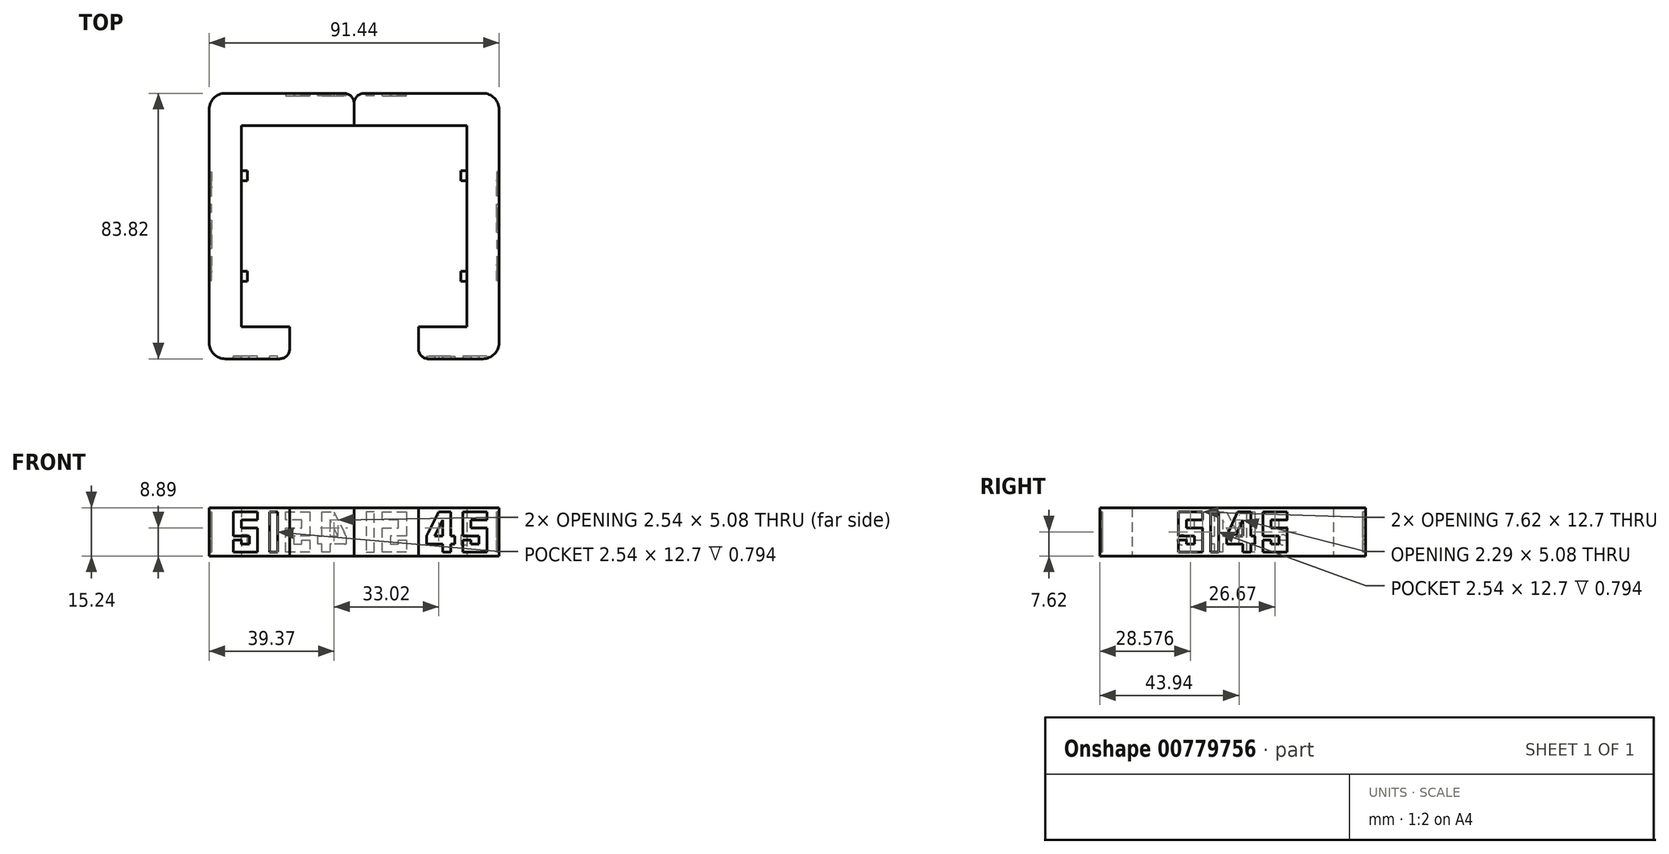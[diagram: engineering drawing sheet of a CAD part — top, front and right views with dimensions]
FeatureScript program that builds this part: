
annotation { "Feature Type Name" : "Feature", "Feature Type Description" : "" }
export const myFeature = defineFeature(function(context is Context, id is Id, definition is map)
    precondition{}
    {
        {
            var Q0;
            Q0=qCreatedBy(makeId("Top.planeOp"),FACE);
            var sketch = newSketch(context, id + "F0", { "sketchPlane" : qUnion([Q0])});
            skLineSegment(sketch, "E0", {"start": v(0, 28.67) * mm, "end": v(0, 38.83) * mm});
            skLineSegment(sketch, "E1", {"start": v(0, 38.83) * mm, "end": v(45.72, 38.83) * mm});
            skLineSegment(sketch, "E2", {"start": v(45.72, 38.83) * mm, "end": v(45.72, -44.99) * mm});
            skLineSegment(sketch, "E3", {"start": v(45.72, -44.99) * mm, "end": v(20.32, -44.99) * mm});
            skLineSegment(sketch, "E4", {"start": v(20.32, -44.99) * mm, "end": v(20.32, -34.83) * mm});
            skLineSegment(sketch, "E5", {"start": v(20.32, -34.83) * mm, "end": v(35.56, -34.83) * mm});
            skLineSegment(sketch, "E6", {"start": v(35.56, -34.83) * mm, "end": v(35.56, 28.67) * mm});
            skLineSegment(sketch, "E7", {"start": v(35.56, 28.67) * mm, "end": v(0, 28.67) * mm});
            skSolve(sketch);
        }
        {
            var Q0;
            Q0=makeQuery(id+"F0.imprint","IMPRINT",FACE,{"disambiguationData":[TD([[makeQuery(id+"F0.imprint","IMPRINT",EDGE,{"derivedFrom":sQuery(id+"F0.wireOp",EDGE,"E0")}),-1.0]])]});
            extrude(context, id + "F1", {"entities" : qUnion([Q0]), "depth" : 15.24 * mm, "offsetDistance" : 25.4 * mm});
        }
        {
            var Q0;
            Q0=makeQuery(id+"F1.opExtrude","SWEPT_FACE",FACE,{"disambiguationData":[OSD([sQuery(id+"F0.wireOp",EDGE,"E6")])]});
            var sketch = newSketch(context, id + "F2", { "sketchPlane" : qUnion([Q0])});
            skCircle(sketch, "E8", {"center": v(-12.8, 5.08) * mm, "radius": 1.59 * mm});
            skPoint(sketch, "E8.centerSnap0", {"position": v(-28.67, 5.08) * mm});
            skCircle(sketch, "E9", {"center": v(18.95, 5.08) * mm, "radius": 1.59 * mm});
            skPoint(sketch, "E9.centerSnap0", {"position": v(34.83, 5.08) * mm});
            skSolve(sketch);
        }
        {
            var Q0;
            Q0=makeQuery(id+"F2.imprint","IMPRINT",FACE,{"disambiguationData":[TD([[makeQuery(id+"F2.imprint","IMPRINT",EDGE,{"derivedFrom":sQuery(id+"F2.wireOp",EDGE,"E8")}),1.0]])]});
            var Q1;
            Q1=makeQuery(id+"F2.imprint","IMPRINT",FACE,{"disambiguationData":[TD([[makeQuery(id+"F2.imprint","IMPRINT",EDGE,{"derivedFrom":sQuery(id+"F2.wireOp",EDGE,"E9")}),1.0]])]});
            extrude(context, id + "F3", {"entities" : qUnion([Q0, Q1]), "operationType" : NewBodyOperationType.ADD, "depth" : 1.9 * mm, "offsetDistance" : 25.4 * mm});
        }
        {
            var Q0;
            Q0=qCreatedBy(makeId("Top.planeOp"),FACE);
            var sketch = newSketch(context, id + "F4", { "sketchPlane" : qUnion([Q0])});
            skLineSegment(sketch, "E10", {"start": v(0, 28.67) * mm, "end": v(-35.56, 28.67) * mm});
            skLineSegment(sketch, "E11", {"start": v(-35.56, 28.67) * mm, "end": v(-35.56, -34.83) * mm});
            skLineSegment(sketch, "E12", {"start": v(-35.56, -34.83) * mm, "end": v(-20.32, -34.83) * mm});
            skLineSegment(sketch, "E13", {"start": v(-20.32, -34.83) * mm, "end": v(-20.32, -44.99) * mm});
            skLineSegment(sketch, "E14", {"start": v(-20.32, -44.99) * mm, "end": v(-45.72, -44.99) * mm});
            skLineSegment(sketch, "E15", {"start": v(-45.72, -44.99) * mm, "end": v(-45.72, 38.83) * mm});
            skLineSegment(sketch, "E16", {"start": v(-45.72, 38.83) * mm, "end": v(0, 38.83) * mm});
            skLineSegment(sketch, "E17", {"start": v(0, 38.83) * mm, "end": v(0, 28.67) * mm});
            skSolve(sketch);
        }
        {
            var Q0;
            Q0=makeQuery(id+"F4.imprint","IMPRINT",FACE,{"disambiguationData":[TD([[makeQuery(id+"F4.imprint","IMPRINT",EDGE,{"derivedFrom":sQuery(id+"F4.wireOp",EDGE,"E10")}),-1.0]])]});
            extrude(context, id + "F5", {"entities" : qUnion([Q0]), "depth" : 15.24 * mm, "offsetDistance" : 25.4 * mm});
        }
        {
            var Q0;
            Q0=makeQuery(id+"F5.opExtrude","SWEPT_FACE",FACE,{"disambiguationData":[OSD([sQuery(id+"F4.wireOp",EDGE,"E11")])]});
            var sketch = newSketch(context, id + "F6", { "sketchPlane" : qUnion([Q0])});
            skCircle(sketch, "E18", {"center": v(-18.95, 5.08) * mm, "radius": 1.59 * mm});
            skPoint(sketch, "E18.centerSnap0", {"position": v(-34.83, 7.62) * mm});
            skCircle(sketch, "E19", {"center": v(12.8, 5.08) * mm, "radius": 1.59 * mm});
            skSolve(sketch);
        }
        {
            var Q0;
            Q0=makeQuery(id+"F6.imprint","IMPRINT",FACE,{"disambiguationData":[TD([[makeQuery(id+"F6.imprint","IMPRINT",EDGE,{"derivedFrom":sQuery(id+"F6.wireOp",EDGE,"E19")}),1.0]])]});
            var Q1;
            Q1=makeQuery(id+"F6.imprint","IMPRINT",FACE,{"disambiguationData":[TD([[makeQuery(id+"F6.imprint","IMPRINT",EDGE,{"derivedFrom":sQuery(id+"F6.wireOp",EDGE,"E18")}),1.0]])]});
            extrude(context, id + "F7", {"entities" : qUnion([Q0, Q1]), "operationType" : NewBodyOperationType.ADD, "depth" : 1.9 * mm, "offsetDistance" : 25.4 * mm});
        }
        {
            var Q0;
            Q0=makeQuery(id+"F1.opExtrude","SWEPT_FACE",FACE,{"disambiguationData":[OSD([sQuery(id+"F0.wireOp",EDGE,"E2")])]});
            var sketch = newSketch(context, id + "F8", { "sketchPlane" : qUnion([Q0])});
            skLineSegment(sketch, "E20", {"start": v(-12.6, 13.97) * mm, "end": v(-20.22, 13.97) * mm});
            skLineSegment(sketch, "E21", {"start": v(-20.22, 13.97) * mm, "end": v(-20.22, 6.35) * mm});
            skLineSegment(sketch, "E22", {"start": v(-20.22, 6.35) * mm, "end": v(-15.14, 6.35) * mm});
            skLineSegment(sketch, "E23", {"start": v(-15.14, 6.35) * mm, "end": v(-15.14, 3.81) * mm});
            skLineSegment(sketch, "E24", {"start": v(-15.14, 3.8) * mm, "end": v(-17.68, 3.8) * mm});
            skLineSegment(sketch, "E25", {"start": v(-17.68, 3.81) * mm, "end": v(-17.68, 5.08) * mm});
            skLineSegment(sketch, "E26", {"start": v(-17.68, 5.08) * mm, "end": v(-20.22, 5.08) * mm});
            skLineSegment(sketch, "E27", {"start": v(-20.22, 5.08) * mm, "end": v(-20.22, 1.27) * mm});
            skLineSegment(sketch, "E28", {"start": v(-20.22, 1.27) * mm, "end": v(-12.6, 1.27) * mm});
            skLineSegment(sketch, "E29", {"start": v(-12.6, 1.27) * mm, "end": v(-12.6, 8.9) * mm});
            skLineSegment(sketch, "E30", {"start": v(-12.6, 8.89) * mm, "end": v(-17.68, 8.89) * mm});
            skLineSegment(sketch, "E31", {"start": v(-17.68, 8.9) * mm, "end": v(-17.68, 11.43) * mm});
            skLineSegment(sketch, "E32", {"start": v(-17.68, 11.43) * mm, "end": v(-12.6, 11.43) * mm});
            skLineSegment(sketch, "E33", {"start": v(-12.6, 11.43) * mm, "end": v(-12.6, 13.97) * mm});
            skLineSegment(sketch, "E34", {"start": v(-10.06, 13.97) * mm, "end": v(-10.06, 1.27) * mm});
            skLineSegment(sketch, "E35", {"start": v(-10.06, 1.27) * mm, "end": v(-7.52, 1.27) * mm});
            skLineSegment(sketch, "E36", {"start": v(-7.52, 1.27) * mm, "end": v(-7.52, 13.97) * mm});
            skLineSegment(sketch, "E37", {"start": v(-7.52, 13.97) * mm, "end": v(-10.06, 13.97) * mm});
            skLineSegment(sketch, "E38", {"start": v(-1.54, 13.97) * mm, "end": v(-4.98, 6.35) * mm});
            skLineSegment(sketch, "E39", {"start": v(-4.98, 6.35) * mm, "end": v(-4.98, 3.81) * mm});
            skLineSegment(sketch, "E40", {"start": v(-4.98, 3.81) * mm, "end": v(0.1, 3.81) * mm});
            skLineSegment(sketch, "E41", {"start": v(0.1, 3.81) * mm, "end": v(0.1, 1.27) * mm});
            skLineSegment(sketch, "E42", {"start": v(0.1, 1.27) * mm, "end": v(2.64, 1.27) * mm});
            skLineSegment(sketch, "E43", {"start": v(2.64, 1.27) * mm, "end": v(2.64, 3.81) * mm});
            skLineSegment(sketch, "E44", {"start": v(2.64, 3.81) * mm, "end": v(3.9, 3.81) * mm});
            skLineSegment(sketch, "E45", {"start": v(3.9, 3.81) * mm, "end": v(3.9, 6.35) * mm});
            skLineSegment(sketch, "E46", {"start": v(3.9, 6.35) * mm, "end": v(2.64, 6.35) * mm});
            skLineSegment(sketch, "E47", {"start": v(2.64, 6.35) * mm, "end": v(2.64, 13.97) * mm});
            skLineSegment(sketch, "E48", {"start": v(2.64, 13.97) * mm, "end": v(-1.54, 13.97) * mm});
            skLineSegment(sketch, "E49", {"start": v(0.1, 6.35) * mm, "end": v(-2.2, 6.35) * mm});
            skLineSegment(sketch, "E50", {"start": v(-2.2, 6.35) * mm, "end": v(0.1, 11.43) * mm});
            skLineSegment(sketch, "E51", {"start": v(0.1, 11.43) * mm, "end": v(0.1, 6.35) * mm});
            skLineSegment(sketch, "E52", {"start": v(14.07, 13.97) * mm, "end": v(6.45, 13.97) * mm});
            skLineSegment(sketch, "E53", {"start": v(6.45, 13.97) * mm, "end": v(6.45, 6.35) * mm});
            skLineSegment(sketch, "E54", {"start": v(6.45, 6.35) * mm, "end": v(11.53, 6.35) * mm});
            skLineSegment(sketch, "E55", {"start": v(11.53, 6.35) * mm, "end": v(11.53, 3.81) * mm});
            skLineSegment(sketch, "E56", {"start": v(11.53, 3.81) * mm, "end": v(8.99, 3.81) * mm});
            skPoint(sketch, "E56.endSnap0", {"position": v(8.99, 6.35) * mm});
            skLineSegment(sketch, "E57", {"start": v(8.99, 3.81) * mm, "end": v(8.99, 5.08) * mm});
            skPoint(sketch, "E57.endSnap0", {"position": v(11.53, 5.08) * mm});
            skLineSegment(sketch, "E58", {"start": v(8.99, 5.08) * mm, "end": v(6.45, 5.08) * mm});
            skLineSegment(sketch, "E59", {"start": v(6.45, 5.08) * mm, "end": v(6.45, 1.27) * mm});
            skLineSegment(sketch, "E60", {"start": v(6.45, 1.27) * mm, "end": v(14.07, 1.27) * mm});
            skLineSegment(sketch, "E61", {"start": v(14.07, 1.27) * mm, "end": v(14.07, 8.9) * mm});
            skLineSegment(sketch, "E62", {"start": v(14.07, 8.9) * mm, "end": v(8.99, 8.9) * mm});
            skLineSegment(sketch, "E63", {"start": v(8.99, 8.9) * mm, "end": v(8.99, 11.43) * mm});
            skLineSegment(sketch, "E64", {"start": v(8.99, 11.43) * mm, "end": v(14.07, 11.43) * mm});
            skLineSegment(sketch, "E65", {"start": v(14.07, 11.43) * mm, "end": v(14.07, 13.97) * mm});
            skLineSegment(sketch, "E66", {"start": v(-20.22, 13.97) * mm, "end": v(-44.99, 13.97) * mm});
            skLineSegment(sketch, "E67", {"start": v(14.07, 13.97) * mm, "end": v(38.83, 13.97) * mm});
            skSolve(sketch);
        }
        {
            var Q0;
            Q0=makeQuery(id+"F8.imprint","IMPRINT",FACE,{"disambiguationData":[TD([[makeQuery(id+"F8.imprint","IMPRINT",EDGE,{"derivedFrom":sQuery(id+"F8.wireOp",EDGE,"E20")}),1.0]])]});
            var Q1;
            Q1=makeQuery(id+"F8.imprint","IMPRINT",FACE,{"disambiguationData":[TD([[makeQuery(id+"F8.imprint","IMPRINT",EDGE,{"derivedFrom":sQuery(id+"F8.wireOp",EDGE,"E34")}),1.0]])]});
            var Q2;
            Q2=makeQuery(id+"F8.imprint","IMPRINT",FACE,{"disambiguationData":[TD([[makeQuery(id+"F8.imprint","IMPRINT",EDGE,{"derivedFrom":sQuery(id+"F8.wireOp",EDGE,"E38")}),1.0]])]});
            var Q3;
            Q3=makeQuery(id+"F8.imprint","IMPRINT",FACE,{"disambiguationData":[TD([[makeQuery(id+"F8.imprint","IMPRINT",EDGE,{"derivedFrom":sQuery(id+"F8.wireOp",EDGE,"E52")}),1.0]])]});
            extrude(context, id + "F9", {"entities" : qUnion([Q0, Q1, Q2, Q3]), "operationType" : NewBodyOperationType.REMOVE, "oppositeDirection" : true, "depth" : 0.8 * mm, "offsetDistance" : 25.4 * mm});
        }
        {
            var Q0;
            Q0=makeQuery(id+"F1.opExtrude","SWEPT_FACE",FACE,{"disambiguationData":[OSD([sQuery(id+"F0.wireOp",EDGE,"E3")])]});
            var sketch = newSketch(context, id + "F10", { "sketchPlane" : qUnion([Q0])});
            skLineSegment(sketch, "E68", {"start": v(22.86, 6.35) * mm, "end": v(22.86, 3.81) * mm});
            skLineSegment(sketch, "E69", {"start": v(22.86, 3.81) * mm, "end": v(27.94, 3.81) * mm});
            skLineSegment(sketch, "E70", {"start": v(27.94, 3.81) * mm, "end": v(27.94, 1.27) * mm});
            skLineSegment(sketch, "E71", {"start": v(27.94, 1.27) * mm, "end": v(30.48, 1.27) * mm});
            skLineSegment(sketch, "E72", {"start": v(30.48, 1.27) * mm, "end": v(30.48, 3.81) * mm});
            skLineSegment(sketch, "E73", {"start": v(30.48, 3.81) * mm, "end": v(31.75, 3.81) * mm});
            skLineSegment(sketch, "E74", {"start": v(31.75, 3.81) * mm, "end": v(31.75, 6.35) * mm});
            skLineSegment(sketch, "E75", {"start": v(31.75, 6.35) * mm, "end": v(30.48, 6.35) * mm});
            skLineSegment(sketch, "E76", {"start": v(30.48, 6.35) * mm, "end": v(30.48, 13.97) * mm});
            skLineSegment(sketch, "E77", {"start": v(30.48, 13.97) * mm, "end": v(26.67, 13.97) * mm});
            skLineSegment(sketch, "E78", {"start": v(26.67, 13.97) * mm, "end": v(22.86, 6.35) * mm});
            skLineSegment(sketch, "E79", {"start": v(27.94, 6.35) * mm, "end": v(25.4, 6.35) * mm});
            skLineSegment(sketch, "E80", {"start": v(25.4, 6.35) * mm, "end": v(27.94, 11.43) * mm});
            skLineSegment(sketch, "E81", {"start": v(27.94, 11.43) * mm, "end": v(27.94, 6.35) * mm});
            skLineSegment(sketch, "E82", {"start": v(41.91, 13.97) * mm, "end": v(34.3, 13.97) * mm});
            skLineSegment(sketch, "E83", {"start": v(34.3, 13.97) * mm, "end": v(34.3, 6.35) * mm});
            skLineSegment(sketch, "E84", {"start": v(34.3, 6.35) * mm, "end": v(39.37, 6.35) * mm});
            skLineSegment(sketch, "E85", {"start": v(39.37, 6.35) * mm, "end": v(39.37, 3.81) * mm});
            skLineSegment(sketch, "E86", {"start": v(39.37, 3.81) * mm, "end": v(36.83, 3.81) * mm});
            skPoint(sketch, "E86.endSnap0", {"position": v(36.83, 6.35) * mm});
            skLineSegment(sketch, "E87", {"start": v(36.83, 3.81) * mm, "end": v(36.83, 5.08) * mm});
            skPoint(sketch, "E87.endSnap0", {"position": v(39.37, 5.08) * mm});
            skLineSegment(sketch, "E88", {"start": v(36.83, 5.08) * mm, "end": v(34.3, 5.08) * mm});
            skLineSegment(sketch, "E89", {"start": v(34.3, 5.08) * mm, "end": v(34.3, 1.27) * mm});
            skLineSegment(sketch, "E90", {"start": v(34.3, 1.27) * mm, "end": v(41.91, 1.27) * mm});
            skLineSegment(sketch, "E91", {"start": v(41.91, 1.27) * mm, "end": v(41.91, 8.89) * mm});
            skLineSegment(sketch, "E92", {"start": v(41.91, 8.89) * mm, "end": v(36.83, 8.89) * mm});
            skLineSegment(sketch, "E93", {"start": v(36.83, 8.89) * mm, "end": v(36.83, 11.43) * mm});
            skLineSegment(sketch, "E94", {"start": v(36.83, 11.43) * mm, "end": v(41.91, 11.43) * mm});
            skLineSegment(sketch, "E95", {"start": v(41.91, 11.43) * mm, "end": v(41.91, 13.97) * mm});
            skSolve(sketch);
        }
        {
            var Q0;
            Q0=makeQuery(id+"F10.imprint","IMPRINT",FACE,{"disambiguationData":[TD([[makeQuery(id+"F10.imprint","IMPRINT",EDGE,{"derivedFrom":sQuery(id+"F10.wireOp",EDGE,"E68")}),1.0]])]});
            var Q1;
            Q1=makeQuery(id+"F10.imprint","IMPRINT",FACE,{"disambiguationData":[TD([[makeQuery(id+"F10.imprint","IMPRINT",EDGE,{"derivedFrom":sQuery(id+"F10.wireOp",EDGE,"E82")}),1.0]])]});
            extrude(context, id + "F11", {"entities" : qUnion([Q0, Q1]), "operationType" : NewBodyOperationType.REMOVE, "oppositeDirection" : true, "depth" : 0.8 * mm, "offsetDistance" : 25.4 * mm});
        }
        {
            var Q0;
            Q0=makeQuery(id+"F5.opExtrude","SWEPT_FACE",FACE,{"disambiguationData":[OSD([sQuery(id+"F4.wireOp",EDGE,"E14")])]});
            var sketch = newSketch(context, id + "F12", { "sketchPlane" : qUnion([Q0])});
            skLineSegment(sketch, "E96", {"start": v(-24.13, 13.97) * mm, "end": v(-26.67, 13.97) * mm});
            skLineSegment(sketch, "E97", {"start": v(-26.67, 13.97) * mm, "end": v(-26.67, 1.27) * mm});
            skLineSegment(sketch, "E98", {"start": v(-26.67, 1.27) * mm, "end": v(-24.13, 1.27) * mm});
            skLineSegment(sketch, "E99", {"start": v(-24.13, 1.27) * mm, "end": v(-24.13, 13.97) * mm});
            skLineSegment(sketch, "E100", {"start": v(-30.48, 13.97) * mm, "end": v(-38.1, 13.97) * mm});
            skLineSegment(sketch, "E101", {"start": v(-38.1, 13.97) * mm, "end": v(-38.1, 6.35) * mm});
            skLineSegment(sketch, "E102", {"start": v(-38.1, 6.35) * mm, "end": v(-33.02, 6.35) * mm});
            skLineSegment(sketch, "E103", {"start": v(-33.02, 6.35) * mm, "end": v(-33.02, 3.8) * mm});
            skLineSegment(sketch, "E104", {"start": v(-33.02, 3.8) * mm, "end": v(-35.56, 3.8) * mm});
            skLineSegment(sketch, "E105", {"start": v(-35.56, 3.8) * mm, "end": v(-35.56, 5.08) * mm});
            skLineSegment(sketch, "E106", {"start": v(-35.56, 5.08) * mm, "end": v(-38.1, 5.08) * mm});
            skLineSegment(sketch, "E107", {"start": v(-38.1, 5.08) * mm, "end": v(-38.1, 1.27) * mm});
            skLineSegment(sketch, "E108", {"start": v(-38.1, 1.27) * mm, "end": v(-30.48, 1.27) * mm});
            skLineSegment(sketch, "E109", {"start": v(-30.48, 1.27) * mm, "end": v(-30.48, 8.9) * mm});
            skLineSegment(sketch, "E110", {"start": v(-30.48, 8.89) * mm, "end": v(-35.56, 8.89) * mm});
            skLineSegment(sketch, "E111", {"start": v(-35.56, 8.89) * mm, "end": v(-35.56, 11.43) * mm});
            skLineSegment(sketch, "E112", {"start": v(-35.56, 11.43) * mm, "end": v(-30.48, 11.43) * mm});
            skLineSegment(sketch, "E113", {"start": v(-30.48, 11.43) * mm, "end": v(-30.48, 13.97) * mm});
            skSolve(sketch);
        }
        {
            var Q0;
            Q0=makeQuery(id+"F12.imprint","IMPRINT",FACE,{"disambiguationData":[TD([[makeQuery(id+"F12.imprint","IMPRINT",EDGE,{"derivedFrom":sQuery(id+"F12.wireOp",EDGE,"E100")}),1.0]])]});
            var Q1;
            Q1=makeQuery(id+"F12.imprint","IMPRINT",FACE,{"disambiguationData":[TD([[makeQuery(id+"F12.imprint","IMPRINT",EDGE,{"derivedFrom":sQuery(id+"F12.wireOp",EDGE,"E96")}),1.0]])]});
            extrude(context, id + "F13", {"entities" : qUnion([Q0, Q1]), "operationType" : NewBodyOperationType.REMOVE, "oppositeDirection" : true, "depth" : 0.8 * mm, "offsetDistance" : 25.4 * mm});
        }
        {
            var Q0;
            Q0=makeQuery(id+"F5.opExtrude","SWEPT_FACE",FACE,{"disambiguationData":[OSD([sQuery(id+"F4.wireOp",EDGE,"E15")])]});
            var sketch = newSketch(context, id + "F14", { "sketchPlane" : qUnion([Q0])});
            skLineSegment(sketch, "E114", {"start": v(-6.45, 13.97) * mm, "end": v(-14.07, 13.97) * mm});
            skLineSegment(sketch, "E115", {"start": v(-14.07, 13.97) * mm, "end": v(-14.07, 6.35) * mm});
            skLineSegment(sketch, "E116", {"start": v(-14.07, 6.35) * mm, "end": v(-8.99, 6.35) * mm});
            skLineSegment(sketch, "E117", {"start": v(-8.99, 6.35) * mm, "end": v(-8.99, 3.8) * mm});
            skLineSegment(sketch, "E118", {"start": v(-8.99, 3.81) * mm, "end": v(-11.53, 3.81) * mm});
            skLineSegment(sketch, "E119", {"start": v(-11.53, 3.8) * mm, "end": v(-11.53, 5.08) * mm});
            skLineSegment(sketch, "E120", {"start": v(-11.53, 5.08) * mm, "end": v(-14.07, 5.08) * mm});
            skLineSegment(sketch, "E121", {"start": v(-14.07, 5.08) * mm, "end": v(-14.07, 1.27) * mm});
            skLineSegment(sketch, "E122", {"start": v(-14.07, 1.27) * mm, "end": v(-6.45, 1.27) * mm});
            skLineSegment(sketch, "E123", {"start": v(-6.45, 1.27) * mm, "end": v(-6.45, 8.9) * mm});
            skLineSegment(sketch, "E124", {"start": v(-6.45, 8.9) * mm, "end": v(-11.53, 8.9) * mm});
            skLineSegment(sketch, "E125", {"start": v(-11.53, 8.89) * mm, "end": v(-11.53, 11.43) * mm});
            skLineSegment(sketch, "E126", {"start": v(-11.53, 11.43) * mm, "end": v(-6.45, 11.43) * mm});
            skLineSegment(sketch, "E127", {"start": v(-6.45, 11.43) * mm, "end": v(-6.45, 13.97) * mm});
            skLineSegment(sketch, "E128", {"start": v(-3.9, 13.97) * mm, "end": v(-3.9, 1.27) * mm});
            skLineSegment(sketch, "E129", {"start": v(-3.9, 1.27) * mm, "end": v(-1.37, 1.27) * mm});
            skLineSegment(sketch, "E130", {"start": v(-1.37, 1.27) * mm, "end": v(-1.37, 13.97) * mm});
            skLineSegment(sketch, "E131", {"start": v(-1.37, 13.97) * mm, "end": v(-3.9, 13.97) * mm});
            skLineSegment(sketch, "E132", {"start": v(4.98, 13.97) * mm, "end": v(1.17, 6.35) * mm});
            skLineSegment(sketch, "E133", {"start": v(1.17, 6.35) * mm, "end": v(1.17, 3.81) * mm});
            skLineSegment(sketch, "E134", {"start": v(1.17, 3.81) * mm, "end": v(6.25, 3.81) * mm});
            skLineSegment(sketch, "E135", {"start": v(6.25, 3.81) * mm, "end": v(6.25, 1.27) * mm});
            skLineSegment(sketch, "E136", {"start": v(6.25, 1.27) * mm, "end": v(8.8, 1.27) * mm});
            skLineSegment(sketch, "E137", {"start": v(8.8, 1.27) * mm, "end": v(8.8, 3.81) * mm});
            skLineSegment(sketch, "E138", {"start": v(8.8, 3.81) * mm, "end": v(10.06, 3.81) * mm});
            skLineSegment(sketch, "E139", {"start": v(10.06, 3.81) * mm, "end": v(10.06, 6.35) * mm});
            skLineSegment(sketch, "E140", {"start": v(10.06, 6.35) * mm, "end": v(8.8, 6.35) * mm});
            skLineSegment(sketch, "E141", {"start": v(8.8, 6.35) * mm, "end": v(8.8, 13.97) * mm});
            skLineSegment(sketch, "E142", {"start": v(8.8, 13.97) * mm, "end": v(4.98, 13.97) * mm});
            skLineSegment(sketch, "E143", {"start": v(6.25, 6.35) * mm, "end": v(3.71, 6.35) * mm});
            skLineSegment(sketch, "E144", {"start": v(3.71, 6.35) * mm, "end": v(6.25, 11.43) * mm});
            skLineSegment(sketch, "E145", {"start": v(6.25, 11.43) * mm, "end": v(6.25, 6.35) * mm});
            skLineSegment(sketch, "E146", {"start": v(20.22, 13.97) * mm, "end": v(12.6, 13.97) * mm});
            skLineSegment(sketch, "E147", {"start": v(12.6, 13.97) * mm, "end": v(12.6, 6.35) * mm});
            skLineSegment(sketch, "E148", {"start": v(12.6, 6.35) * mm, "end": v(17.68, 6.35) * mm});
            skLineSegment(sketch, "E149", {"start": v(17.68, 6.35) * mm, "end": v(17.68, 3.81) * mm});
            skLineSegment(sketch, "E150", {"start": v(17.68, 3.81) * mm, "end": v(15.14, 3.81) * mm});
            skLineSegment(sketch, "E151", {"start": v(15.14, 3.81) * mm, "end": v(15.14, 5.08) * mm});
            skLineSegment(sketch, "E152", {"start": v(15.14, 5.08) * mm, "end": v(12.6, 5.08) * mm});
            skLineSegment(sketch, "E153", {"start": v(12.6, 5.08) * mm, "end": v(12.6, 1.27) * mm});
            skLineSegment(sketch, "E154", {"start": v(12.6, 1.27) * mm, "end": v(20.22, 1.27) * mm});
            skLineSegment(sketch, "E155", {"start": v(20.22, 1.27) * mm, "end": v(20.22, 8.9) * mm});
            skLineSegment(sketch, "E156", {"start": v(20.22, 8.9) * mm, "end": v(15.14, 8.9) * mm});
            skLineSegment(sketch, "E157", {"start": v(15.14, 8.9) * mm, "end": v(15.14, 11.43) * mm});
            skLineSegment(sketch, "E158", {"start": v(15.14, 11.43) * mm, "end": v(20.22, 11.43) * mm});
            skLineSegment(sketch, "E159", {"start": v(20.22, 11.43) * mm, "end": v(20.22, 13.97) * mm});
            skLineSegment(sketch, "E160", {"start": v(-38.83, 13.97) * mm, "end": v(-14.07, 13.97) * mm});
            skLineSegment(sketch, "E161", {"start": v(44.99, 13.97) * mm, "end": v(20.22, 13.97) * mm});
            skSolve(sketch);
        }
        {
            var Q0;
            Q0 = qSketchRegion(id + "F14", true);
            extrude(context, id + "F15", {"entities" : qUnion([Q0]), "operationType" : NewBodyOperationType.REMOVE, "oppositeDirection" : true, "depth" : 0.8 * mm, "offsetDistance" : 25.4 * mm});
        }
        {
            var Q0;
            Q0=makeQuery(id+"F1.opExtrude","SWEPT_FACE",FACE,{"disambiguationData":[OSD([sQuery(id+"F0.wireOp",EDGE,"E1")])]});
            var sketch = newSketch(context, id + "F16", { "sketchPlane" : qUnion([Q0])});
            skLineSegment(sketch, "E162", {"start": v(-8.9, 13.97) * mm, "end": v(-16.51, 13.97) * mm});
            skLineSegment(sketch, "E163", {"start": v(-16.51, 13.97) * mm, "end": v(-16.51, 6.35) * mm});
            skLineSegment(sketch, "E164", {"start": v(-16.51, 6.35) * mm, "end": v(-11.43, 6.35) * mm});
            skLineSegment(sketch, "E165", {"start": v(-11.43, 6.35) * mm, "end": v(-11.43, 3.81) * mm});
            skLineSegment(sketch, "E166", {"start": v(-11.43, 3.81) * mm, "end": v(-13.97, 3.8) * mm});
            skLineSegment(sketch, "E167", {"start": v(-13.97, 3.8) * mm, "end": v(-13.97, 5.08) * mm});
            skLineSegment(sketch, "E168", {"start": v(-13.97, 5.08) * mm, "end": v(-16.51, 5.08) * mm});
            skLineSegment(sketch, "E169", {"start": v(-16.51, 5.08) * mm, "end": v(-16.51, 1.27) * mm});
            skLineSegment(sketch, "E170", {"start": v(-16.51, 1.27) * mm, "end": v(-8.9, 1.27) * mm});
            skLineSegment(sketch, "E171", {"start": v(-8.9, 1.27) * mm, "end": v(-8.9, 8.89) * mm});
            skLineSegment(sketch, "E172", {"start": v(-8.9, 8.9) * mm, "end": v(-13.97, 8.89) * mm});
            skLineSegment(sketch, "E173", {"start": v(-13.97, 8.89) * mm, "end": v(-13.97, 11.43) * mm});
            skLineSegment(sketch, "E174", {"start": v(-13.97, 11.43) * mm, "end": v(-8.9, 11.43) * mm});
            skLineSegment(sketch, "E175", {"start": v(-8.9, 11.43) * mm, "end": v(-8.9, 13.97) * mm});
            skLineSegment(sketch, "E176", {"start": v(-6.35, 13.97) * mm, "end": v(-3.81, 13.97) * mm});
            skLineSegment(sketch, "E177", {"start": v(-3.81, 13.97) * mm, "end": v(-3.81, 1.27) * mm});
            skLineSegment(sketch, "E178", {"start": v(-3.81, 1.27) * mm, "end": v(-6.35, 1.27) * mm});
            skLineSegment(sketch, "E179", {"start": v(-6.35, 1.27) * mm, "end": v(-6.35, 13.97) * mm});
            skSolve(sketch);
        }
        {
            var Q0;
            Q0 = qSketchRegion(id + "F16", true);
            extrude(context, id + "F17", {"entities" : qUnion([Q0]), "operationType" : NewBodyOperationType.REMOVE, "oppositeDirection" : true, "depth" : 0.8 * mm, "offsetDistance" : 25.4 * mm});
        }
        {
            var Q0;
            Q0=makeQuery(id+"F5.opExtrude","SWEPT_FACE",FACE,{"disambiguationData":[OSD([sQuery(id+"F4.wireOp",EDGE,"E16")])]});
            var sketch = newSketch(context, id + "F18", { "sketchPlane" : qUnion([Q0])});
            skLineSegment(sketch, "E180", {"start": v(2.54, 6.35) * mm, "end": v(2.54, 3.81) * mm});
            skLineSegment(sketch, "E181", {"start": v(2.54, 3.81) * mm, "end": v(7.62, 3.81) * mm});
            skLineSegment(sketch, "E182", {"start": v(7.62, 3.81) * mm, "end": v(7.62, 1.27) * mm});
            skLineSegment(sketch, "E183", {"start": v(7.62, 1.27) * mm, "end": v(10.16, 1.27) * mm});
            skLineSegment(sketch, "E184", {"start": v(10.16, 1.27) * mm, "end": v(10.16, 3.81) * mm});
            skLineSegment(sketch, "E185", {"start": v(10.16, 3.81) * mm, "end": v(11.43, 3.81) * mm});
            skLineSegment(sketch, "E186", {"start": v(11.43, 3.81) * mm, "end": v(11.43, 6.35) * mm});
            skLineSegment(sketch, "E187", {"start": v(11.43, 6.35) * mm, "end": v(10.16, 6.35) * mm});
            skLineSegment(sketch, "E188", {"start": v(10.16, 6.35) * mm, "end": v(10.16, 13.97) * mm});
            skLineSegment(sketch, "E189", {"start": v(10.16, 13.97) * mm, "end": v(6.35, 13.97) * mm});
            skLineSegment(sketch, "E190", {"start": v(6.35, 13.97) * mm, "end": v(2.54, 6.35) * mm});
            skLineSegment(sketch, "E191", {"start": v(7.62, 6.35) * mm, "end": v(5.08, 6.35) * mm});
            skLineSegment(sketch, "E192", {"start": v(5.08, 6.35) * mm, "end": v(7.62, 11.43) * mm});
            skLineSegment(sketch, "E193", {"start": v(7.62, 11.43) * mm, "end": v(7.62, 6.35) * mm});
            skLineSegment(sketch, "E194", {"start": v(21.6, 13.97) * mm, "end": v(13.97, 13.97) * mm});
            skLineSegment(sketch, "E195", {"start": v(13.97, 13.97) * mm, "end": v(13.97, 6.35) * mm});
            skLineSegment(sketch, "E196", {"start": v(13.97, 6.35) * mm, "end": v(19.05, 6.35) * mm});
            skLineSegment(sketch, "E197", {"start": v(19.05, 6.35) * mm, "end": v(19.05, 3.81) * mm});
            skLineSegment(sketch, "E198", {"start": v(19.05, 3.81) * mm, "end": v(16.51, 3.81) * mm});
            skLineSegment(sketch, "E199", {"start": v(16.51, 3.81) * mm, "end": v(16.51, 5.08) * mm});
            skLineSegment(sketch, "E200", {"start": v(16.51, 5.08) * mm, "end": v(13.97, 5.08) * mm});
            skLineSegment(sketch, "E201", {"start": v(13.97, 5.08) * mm, "end": v(13.97, 1.27) * mm});
            skLineSegment(sketch, "E202", {"start": v(13.97, 1.27) * mm, "end": v(21.59, 1.27) * mm});
            skLineSegment(sketch, "E203", {"start": v(21.59, 1.27) * mm, "end": v(21.59, 8.9) * mm});
            skLineSegment(sketch, "E204", {"start": v(21.59, 8.9) * mm, "end": v(16.51, 8.9) * mm});
            skLineSegment(sketch, "E205", {"start": v(16.51, 8.9) * mm, "end": v(16.51, 11.43) * mm});
            skLineSegment(sketch, "E206", {"start": v(16.51, 11.43) * mm, "end": v(21.59, 11.43) * mm});
            skLineSegment(sketch, "E207", {"start": v(21.59, 11.43) * mm, "end": v(21.59, 13.97) * mm});
            skSolve(sketch);
        }
        {
            var Q0;
            Q0 = qSketchRegion(id + "F18", true);
            extrude(context, id + "F19", {"entities" : qUnion([Q0]), "operationType" : NewBodyOperationType.REMOVE, "oppositeDirection" : true, "depth" : 0.8 * mm, "offsetDistance" : 25.4 * mm});
        }
        {
            var Q0;
            Q0=makeQuery(id+"F5.opExtrude","SWEPT_EDGE",EDGE,{"disambiguationData":[OSD([sQuery(id+"F4.wireOp",EDGE,"E15"),sQuery(id+"F4.wireOp",EDGE,"E16")])]});
            var Q1;
            Q1=makeQuery(id+"F5.opExtrude","SWEPT_EDGE",EDGE,{"disambiguationData":[OSD([sQuery(id+"F4.wireOp",EDGE,"E14"),sQuery(id+"F4.wireOp",EDGE,"E15")])]});
            fillet(context, id + "F20", {"entities" : qUnion([Q0, Q1]), "tangentPropagation" : true, "radius" : 5.08 * mm, "defaultsChanged" : true, "vertexSettings" : [], "allowEdgeOverflow" : false});
        }
        {
            var Q0;
            Q0=makeQuery(id+"F1.opExtrude","SWEPT_EDGE",EDGE,{"disambiguationData":[OSD([sQuery(id+"F0.wireOp",EDGE,"E2"),sQuery(id+"F0.wireOp",EDGE,"E3")])]});
            var Q1;
            Q1=makeQuery(id+"F1.opExtrude","SWEPT_EDGE",EDGE,{"disambiguationData":[OSD([sQuery(id+"F0.wireOp",EDGE,"E1"),sQuery(id+"F0.wireOp",EDGE,"E2")])]});
            fillet(context, id + "F21", {"entities" : qUnion([Q0, Q1]), "tangentPropagation" : true, "radius" : 5.08 * mm, "defaultsChanged" : false, "vertexSettings" : [], "allowEdgeOverflow" : false});
        }
        {
            var Q0;
            Q0=makeQuery(id+"F1.opExtrude","SWEPT_EDGE",EDGE,{"disambiguationData":[OSD([sQuery(id+"F0.wireOp",EDGE,"E3"),sQuery(id+"F0.wireOp",EDGE,"E4")])]});
            var Q1;
            Q1=makeQuery(id+"F5.opExtrude","SWEPT_EDGE",EDGE,{"disambiguationData":[OSD([sQuery(id+"F4.wireOp",EDGE,"E13"),sQuery(id+"F4.wireOp",EDGE,"E14")])]});
            var Q2;
            Q2=makeQuery(id+"F1.opExtrude","SWEPT_EDGE",EDGE,{"disambiguationData":[OSD([sQuery(id+"F0.wireOp",EDGE,"E0"),sQuery(id+"F0.wireOp",EDGE,"E1")])]});
            var Q3;
            Q3=makeQuery(id+"F5.opExtrude","SWEPT_EDGE",EDGE,{"disambiguationData":[OSD([sQuery(id+"F4.wireOp",EDGE,"E16"),sQuery(id+"F4.wireOp",EDGE,"E17")])]});
            fillet(context, id + "F22", {"entities" : qUnion([Q0, Q1, Q2, Q3]), "tangentPropagation" : true, "radius" : 3.17 * mm, "defaultsChanged" : true, "vertexSettings" : [], "allowEdgeOverflow" : false});
        }
        {
            var Q0;
            Q0=makeQuery(id+"F11.boolean.opBoolean","COPY",FACE,{"derivedFrom":makeQuery(id+"F11.opExtrude","CAP_FACE",FACE,{"disambiguationData":[OSD([sQuery(id+"F10.wireOp",EDGE,"E68"),sQuery(id+"F10.wireOp",EDGE,"E69"),sQuery(id+"F10.wireOp",EDGE,"E70"),sQuery(id+"F10.wireOp",EDGE,"E71"),sQuery(id+"F10.wireOp",EDGE,"E72"),sQuery(id+"F10.wireOp",EDGE,"E73"),sQuery(id+"F10.wireOp",EDGE,"E74"),sQuery(id+"F10.wireOp",EDGE,"E75"),sQuery(id+"F10.wireOp",EDGE,"E76"),sQuery(id+"F10.wireOp",EDGE,"E77"),sQuery(id+"F10.wireOp",EDGE,"E78"),sQuery(id+"F10.wireOp",EDGE,"E79"),sQuery(id+"F10.wireOp",EDGE,"E80"),sQuery(id+"F10.wireOp",EDGE,"E81")])],"isStart":false})});
            var Q1;
            Q1=makeQuery(id+"F11.boolean.opBoolean","COPY",FACE,{"derivedFrom":makeQuery(id+"F11.opExtrude","CAP_FACE",FACE,{"disambiguationData":[OSD([sQuery(id+"F10.wireOp",EDGE,"E82"),sQuery(id+"F10.wireOp",EDGE,"E83"),sQuery(id+"F10.wireOp",EDGE,"E84"),sQuery(id+"F10.wireOp",EDGE,"E85"),sQuery(id+"F10.wireOp",EDGE,"E86"),sQuery(id+"F10.wireOp",EDGE,"E87"),sQuery(id+"F10.wireOp",EDGE,"E88"),sQuery(id+"F10.wireOp",EDGE,"E89"),sQuery(id+"F10.wireOp",EDGE,"E90"),sQuery(id+"F10.wireOp",EDGE,"E91"),sQuery(id+"F10.wireOp",EDGE,"E92"),sQuery(id+"F10.wireOp",EDGE,"E93"),sQuery(id+"F10.wireOp",EDGE,"E94"),sQuery(id+"F10.wireOp",EDGE,"E95")])],"isStart":false})});
            var Q2;
            Q2=makeQuery(id+"F13.boolean.opBoolean","COPY",FACE,{"derivedFrom":makeQuery(id+"F13.opExtrude","CAP_FACE",FACE,{"disambiguationData":[OSD([sQuery(id+"F12.wireOp",EDGE,"E96"),sQuery(id+"F12.wireOp",EDGE,"E97"),sQuery(id+"F12.wireOp",EDGE,"E98"),sQuery(id+"F12.wireOp",EDGE,"E99")])],"isStart":false})});
            var Q3;
            Q3=makeQuery(id+"F13.boolean.opBoolean","COPY",FACE,{"derivedFrom":makeQuery(id+"F13.opExtrude","CAP_FACE",FACE,{"disambiguationData":[OSD([sQuery(id+"F12.wireOp",EDGE,"E100"),sQuery(id+"F12.wireOp",EDGE,"E101"),sQuery(id+"F12.wireOp",EDGE,"E102"),sQuery(id+"F12.wireOp",EDGE,"E103"),sQuery(id+"F12.wireOp",EDGE,"E104"),sQuery(id+"F12.wireOp",EDGE,"E105"),sQuery(id+"F12.wireOp",EDGE,"E106"),sQuery(id+"F12.wireOp",EDGE,"E107"),sQuery(id+"F12.wireOp",EDGE,"E108"),sQuery(id+"F12.wireOp",EDGE,"E109"),sQuery(id+"F12.wireOp",EDGE,"E110"),sQuery(id+"F12.wireOp",EDGE,"E111"),sQuery(id+"F12.wireOp",EDGE,"E112"),sQuery(id+"F12.wireOp",EDGE,"E113")])],"isStart":false})});
            extrude(context, id + "F23", {"entities" : qUnion([Q0, Q1, Q2, Q3]), "depth" : 0.8 * mm, "offsetDistance" : 25.4 * mm});
        }
        {
            var Q0;
            Q0=makeQuery(id+"F15.boolean.opBoolean","COPY",FACE,{"derivedFrom":makeQuery(id+"F15.opExtrude","CAP_FACE",FACE,{"disambiguationData":[OSD([sQuery(id+"F14.wireOp",EDGE,"E114"),sQuery(id+"F14.wireOp",EDGE,"E115"),sQuery(id+"F14.wireOp",EDGE,"E116"),sQuery(id+"F14.wireOp",EDGE,"E117"),sQuery(id+"F14.wireOp",EDGE,"E118"),sQuery(id+"F14.wireOp",EDGE,"E119"),sQuery(id+"F14.wireOp",EDGE,"E120"),sQuery(id+"F14.wireOp",EDGE,"E121"),sQuery(id+"F14.wireOp",EDGE,"E122"),sQuery(id+"F14.wireOp",EDGE,"E123"),sQuery(id+"F14.wireOp",EDGE,"E124"),sQuery(id+"F14.wireOp",EDGE,"E125"),sQuery(id+"F14.wireOp",EDGE,"E126"),sQuery(id+"F14.wireOp",EDGE,"E127")])],"isStart":false})});
            var Q1;
            Q1=makeQuery(id+"F15.boolean.opBoolean","COPY",FACE,{"derivedFrom":makeQuery(id+"F15.opExtrude","CAP_FACE",FACE,{"disambiguationData":[OSD([sQuery(id+"F14.wireOp",EDGE,"E128"),sQuery(id+"F14.wireOp",EDGE,"E129"),sQuery(id+"F14.wireOp",EDGE,"E130"),sQuery(id+"F14.wireOp",EDGE,"E131")])],"isStart":false})});
            var Q2;
            Q2=makeQuery(id+"F15.boolean.opBoolean","COPY",FACE,{"derivedFrom":makeQuery(id+"F15.opExtrude","CAP_FACE",FACE,{"disambiguationData":[OSD([sQuery(id+"F14.wireOp",EDGE,"E132"),sQuery(id+"F14.wireOp",EDGE,"E133"),sQuery(id+"F14.wireOp",EDGE,"E134"),sQuery(id+"F14.wireOp",EDGE,"E135"),sQuery(id+"F14.wireOp",EDGE,"E136"),sQuery(id+"F14.wireOp",EDGE,"E137"),sQuery(id+"F14.wireOp",EDGE,"E138"),sQuery(id+"F14.wireOp",EDGE,"E139"),sQuery(id+"F14.wireOp",EDGE,"E140"),sQuery(id+"F14.wireOp",EDGE,"E141"),sQuery(id+"F14.wireOp",EDGE,"E142"),sQuery(id+"F14.wireOp",EDGE,"E143"),sQuery(id+"F14.wireOp",EDGE,"E144"),sQuery(id+"F14.wireOp",EDGE,"E145")])],"isStart":false})});
            var Q3;
            Q3=makeQuery(id+"F15.boolean.opBoolean","COPY",FACE,{"derivedFrom":makeQuery(id+"F15.opExtrude","CAP_FACE",FACE,{"disambiguationData":[OSD([sQuery(id+"F14.wireOp",EDGE,"E146"),sQuery(id+"F14.wireOp",EDGE,"E147"),sQuery(id+"F14.wireOp",EDGE,"E148"),sQuery(id+"F14.wireOp",EDGE,"E149"),sQuery(id+"F14.wireOp",EDGE,"E150"),sQuery(id+"F14.wireOp",EDGE,"E151"),sQuery(id+"F14.wireOp",EDGE,"E152"),sQuery(id+"F14.wireOp",EDGE,"E153"),sQuery(id+"F14.wireOp",EDGE,"E154"),sQuery(id+"F14.wireOp",EDGE,"E155"),sQuery(id+"F14.wireOp",EDGE,"E156"),sQuery(id+"F14.wireOp",EDGE,"E157"),sQuery(id+"F14.wireOp",EDGE,"E158"),sQuery(id+"F14.wireOp",EDGE,"E159")])],"isStart":false})});
            extrude(context, id + "F24", {"entities" : qUnion([Q0, Q1, Q2, Q3]), "depth" : 0.8 * mm, "offsetDistance" : 25.4 * mm});
        }
        {
            var Q0;
            Q0=makeQuery(id+"F17.boolean.opBoolean","COPY",FACE,{"derivedFrom":makeQuery(id+"F17.opExtrude","CAP_FACE",FACE,{"disambiguationData":[OSD([sQuery(id+"F16.wireOp",EDGE,"E162"),sQuery(id+"F16.wireOp",EDGE,"E163"),sQuery(id+"F16.wireOp",EDGE,"E164"),sQuery(id+"F16.wireOp",EDGE,"E165"),sQuery(id+"F16.wireOp",EDGE,"E166"),sQuery(id+"F16.wireOp",EDGE,"E167"),sQuery(id+"F16.wireOp",EDGE,"E168"),sQuery(id+"F16.wireOp",EDGE,"E169"),sQuery(id+"F16.wireOp",EDGE,"E170"),sQuery(id+"F16.wireOp",EDGE,"E171"),sQuery(id+"F16.wireOp",EDGE,"E172"),sQuery(id+"F16.wireOp",EDGE,"E173"),sQuery(id+"F16.wireOp",EDGE,"E174"),sQuery(id+"F16.wireOp",EDGE,"E175")])],"isStart":false})});
            var Q1;
            Q1=makeQuery(id+"F17.boolean.opBoolean","COPY",FACE,{"derivedFrom":makeQuery(id+"F17.opExtrude","CAP_FACE",FACE,{"disambiguationData":[OSD([sQuery(id+"F16.wireOp",EDGE,"E176"),sQuery(id+"F16.wireOp",EDGE,"E177"),sQuery(id+"F16.wireOp",EDGE,"E178"),sQuery(id+"F16.wireOp",EDGE,"E179")])],"isStart":false})});
            var Q2;
            Q2=makeQuery(id+"F19.boolean.opBoolean","COPY",FACE,{"derivedFrom":makeQuery(id+"F19.opExtrude","CAP_FACE",FACE,{"disambiguationData":[OSD([sQuery(id+"F18.wireOp",EDGE,"E180"),sQuery(id+"F18.wireOp",EDGE,"E181"),sQuery(id+"F18.wireOp",EDGE,"E182"),sQuery(id+"F18.wireOp",EDGE,"E183"),sQuery(id+"F18.wireOp",EDGE,"E184"),sQuery(id+"F18.wireOp",EDGE,"E185"),sQuery(id+"F18.wireOp",EDGE,"E186"),sQuery(id+"F18.wireOp",EDGE,"E187"),sQuery(id+"F18.wireOp",EDGE,"E188"),sQuery(id+"F18.wireOp",EDGE,"E189"),sQuery(id+"F18.wireOp",EDGE,"E190"),sQuery(id+"F18.wireOp",EDGE,"E191"),sQuery(id+"F18.wireOp",EDGE,"E192"),sQuery(id+"F18.wireOp",EDGE,"E193")])],"isStart":false})});
            var Q3;
            Q3=makeQuery(id+"F19.boolean.opBoolean","COPY",FACE,{"derivedFrom":makeQuery(id+"F19.opExtrude","CAP_FACE",FACE,{"disambiguationData":[OSD([sQuery(id+"F18.wireOp",EDGE,"E194"),sQuery(id+"F18.wireOp",EDGE,"E195"),sQuery(id+"F18.wireOp",EDGE,"E196"),sQuery(id+"F18.wireOp",EDGE,"E197"),sQuery(id+"F18.wireOp",EDGE,"E198"),sQuery(id+"F18.wireOp",EDGE,"E199"),sQuery(id+"F18.wireOp",EDGE,"E200"),sQuery(id+"F18.wireOp",EDGE,"E201"),sQuery(id+"F18.wireOp",EDGE,"E202"),sQuery(id+"F18.wireOp",EDGE,"E203"),sQuery(id+"F18.wireOp",EDGE,"E204"),sQuery(id+"F18.wireOp",EDGE,"E205"),sQuery(id+"F18.wireOp",EDGE,"E206"),sQuery(id+"F18.wireOp",EDGE,"E207")])],"isStart":false})});
            extrude(context, id + "F25", {"entities" : qUnion([Q0, Q1, Q2, Q3]), "depth" : 0.8 * mm, "offsetDistance" : 25.4 * mm});
        }
        {
            var Q0;
            Q0=makeQuery(id+"F9.boolean.opBoolean","COPY",FACE,{"derivedFrom":makeQuery(id+"F9.opExtrude","CAP_FACE",FACE,{"disambiguationData":[OSD([sQuery(id+"F8.wireOp",EDGE,"E20"),sQuery(id+"F8.wireOp",EDGE,"E21"),sQuery(id+"F8.wireOp",EDGE,"E22"),sQuery(id+"F8.wireOp",EDGE,"E23"),sQuery(id+"F8.wireOp",EDGE,"E24"),sQuery(id+"F8.wireOp",EDGE,"E25"),sQuery(id+"F8.wireOp",EDGE,"E26"),sQuery(id+"F8.wireOp",EDGE,"E27"),sQuery(id+"F8.wireOp",EDGE,"E28"),sQuery(id+"F8.wireOp",EDGE,"E29"),sQuery(id+"F8.wireOp",EDGE,"E30"),sQuery(id+"F8.wireOp",EDGE,"E31"),sQuery(id+"F8.wireOp",EDGE,"E32"),sQuery(id+"F8.wireOp",EDGE,"E33")])],"isStart":false})});
            var Q1;
            Q1=makeQuery(id+"F9.boolean.opBoolean","COPY",FACE,{"derivedFrom":makeQuery(id+"F9.opExtrude","CAP_FACE",FACE,{"disambiguationData":[OSD([sQuery(id+"F8.wireOp",EDGE,"E34"),sQuery(id+"F8.wireOp",EDGE,"E35"),sQuery(id+"F8.wireOp",EDGE,"E36"),sQuery(id+"F8.wireOp",EDGE,"E37")])],"isStart":false})});
            var Q2;
            Q2=makeQuery(id+"F9.boolean.opBoolean","COPY",FACE,{"derivedFrom":makeQuery(id+"F9.opExtrude","CAP_FACE",FACE,{"disambiguationData":[OSD([sQuery(id+"F8.wireOp",EDGE,"E38"),sQuery(id+"F8.wireOp",EDGE,"E39"),sQuery(id+"F8.wireOp",EDGE,"E40"),sQuery(id+"F8.wireOp",EDGE,"E41"),sQuery(id+"F8.wireOp",EDGE,"E42"),sQuery(id+"F8.wireOp",EDGE,"E43"),sQuery(id+"F8.wireOp",EDGE,"E44"),sQuery(id+"F8.wireOp",EDGE,"E45"),sQuery(id+"F8.wireOp",EDGE,"E46"),sQuery(id+"F8.wireOp",EDGE,"E47"),sQuery(id+"F8.wireOp",EDGE,"E48"),sQuery(id+"F8.wireOp",EDGE,"E49"),sQuery(id+"F8.wireOp",EDGE,"E50"),sQuery(id+"F8.wireOp",EDGE,"E51")])],"isStart":false})});
            var Q3;
            Q3=makeQuery(id+"F9.boolean.opBoolean","COPY",FACE,{"derivedFrom":makeQuery(id+"F9.opExtrude","CAP_FACE",FACE,{"disambiguationData":[OSD([sQuery(id+"F8.wireOp",EDGE,"E52"),sQuery(id+"F8.wireOp",EDGE,"E53"),sQuery(id+"F8.wireOp",EDGE,"E54"),sQuery(id+"F8.wireOp",EDGE,"E55"),sQuery(id+"F8.wireOp",EDGE,"E56"),sQuery(id+"F8.wireOp",EDGE,"E57"),sQuery(id+"F8.wireOp",EDGE,"E58"),sQuery(id+"F8.wireOp",EDGE,"E59"),sQuery(id+"F8.wireOp",EDGE,"E60"),sQuery(id+"F8.wireOp",EDGE,"E61"),sQuery(id+"F8.wireOp",EDGE,"E62"),sQuery(id+"F8.wireOp",EDGE,"E63"),sQuery(id+"F8.wireOp",EDGE,"E64"),sQuery(id+"F8.wireOp",EDGE,"E65")])],"isStart":false})});
            extrude(context, id + "F26", {"entities" : qUnion([Q0, Q1, Q2, Q3]), "depth" : 0.8 * mm, "offsetDistance" : 25.4 * mm});
        }
        {
            var Q0;
            Q0=makeQuery(id+"F23.opExtrude","SWEPT_FACE",FACE,{"disambiguationData":[OSD([sQuery(id+"F10.wireOp",EDGE,"E90")])]});
            var sketch = newSketch(context, id + "F27", { "sketchPlane" : qUnion([Q0])});
            skArc(sketch, "E208", {"start": v(41.91, 44.83) * mm, "mid": v(41.28, 44.95) * mm, "end": v(40.64, 44.99) * mm});
            skSolve(sketch);
        }
        {
            var Q0;
            {var subQ0=sQuery(id+"F27.wireOp",EDGE,"E208");Q0=makeQuery(id+"F27.imprint","IMPRINT",FACE,{"disambiguationData":[TD([[makeQuery(id+"F27.imprint","IMPRINT",EDGE,{"derivedFrom":subQ0}),-1.0]])]});}
            extrude(context, id + "F28", {"entities" : qUnion([Q0]), "operationType" : NewBodyOperationType.REMOVE, "oppositeDirection" : true, "depth" : 25.4 * mm, "offsetDistance" : 25.4 * mm});
        }
        {
            var Q0;
            Q0=makeQuery(id+"F23.opExtrude","SWEPT_FACE",FACE,{"disambiguationData":[OSD([sQuery(id+"F10.wireOp",EDGE,"E69")])]});
            var sketch = newSketch(context, id + "F29", { "sketchPlane" : qUnion([Q0])});
            skArc(sketch, "E209", {"start": v(23.5, 44.99) * mm, "mid": v(23.18, 44.97) * mm, "end": v(22.86, 44.92) * mm});
            skSolve(sketch);
        }
        {
            var Q0;
            {var subQ0=sQuery(id+"F29.wireOp",EDGE,"E209");Q0=makeQuery(id+"F29.imprint","IMPRINT",FACE,{"disambiguationData":[TD([[makeQuery(id+"F29.imprint","IMPRINT",EDGE,{"derivedFrom":subQ0}),-1.0]])]});}
            extrude(context, id + "F30", {"entities" : qUnion([Q0]), "operationType" : NewBodyOperationType.REMOVE, "oppositeDirection" : true, "depth" : 25.4 * mm, "offsetDistance" : 25.4 * mm});
        }
        {
            var Q0;
            Q0=makeQuery(id+"F25.opExtrude","SWEPT_FACE",FACE,{"disambiguationData":[OSD([sQuery(id+"F18.wireOp",EDGE,"E181")])]});
            var sketch = newSketch(context, id + "F31", { "sketchPlane" : qUnion([Q0])});
            skArc(sketch, "E210", {"start": v(-3.18, -38.83) * mm, "mid": v(-2.86, -38.82) * mm, "end": v(-2.54, -38.77) * mm});
            skSolve(sketch);
        }
        {
            var Q0;
            {var subQ0=sQuery(id+"F31.wireOp",EDGE,"E210");Q0=makeQuery(id+"F31.imprint","IMPRINT",FACE,{"disambiguationData":[TD([[makeQuery(id+"F31.imprint","IMPRINT",EDGE,{"derivedFrom":subQ0}),-1.0]])]});}
            extrude(context, id + "F32", {"entities" : qUnion([Q0]), "operationType" : NewBodyOperationType.REMOVE, "oppositeDirection" : true, "depth" : 25.4 * mm, "offsetDistance" : 25.4 * mm});
        }
    });
